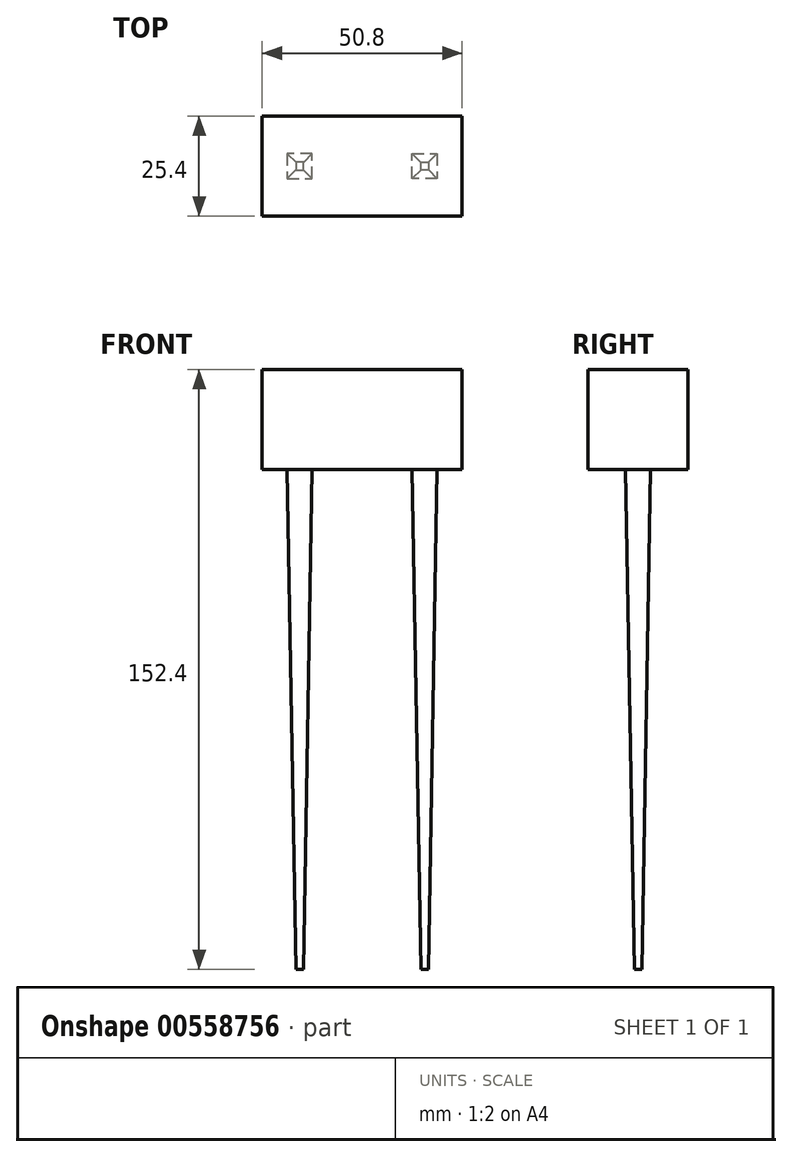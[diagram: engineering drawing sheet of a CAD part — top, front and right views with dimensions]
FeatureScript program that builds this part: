
annotation { "Feature Type Name" : "Feature", "Feature Type Description" : "" }
export const myFeature = defineFeature(function(context is Context, id is Id, definition is map)
    precondition{}
    {
        {
            var Q0;
            Q0=qCreatedBy(makeId("Top.planeOp"),FACE);
            var sketch = newSketch(context, id + "F0", { "sketchPlane" : qUnion([Q0])});
            skLineSegment(sketch, "E0.bottom", {"start": v(-25.4, 12.7) * mm, "end": v(25.4, 12.7) * mm});
            skLineSegment(sketch, "E0.top", {"start": v(-25.4, -12.7) * mm, "end": v(25.4, -12.7) * mm});
            skLineSegment(sketch, "E0.left", {"start": v(-25.4, 12.7) * mm, "end": v(-25.4, -12.7) * mm});
            skLineSegment(sketch, "E0.right", {"start": v(25.4, 12.7) * mm, "end": v(25.4, -12.7) * mm});
            skSolve(sketch);
        }
        {
            var Q0;
            Q0=makeQuery(id+"F0.imprint","IMPRINT",FACE,{"disambiguationData":[TD([[makeQuery(id+"F0.imprint","IMPRINT",EDGE,{"derivedFrom":sQuery(id+"F0.wireOp",EDGE,"E0.bottom")}),-1.0]])]});
            extrude(context, id + "F1", {"entities" : qUnion([Q0]), "oppositeDirection" : true, "depth" : 25.4 * mm, "offsetDistance" : 25.4 * mm});
        }
        {
            var Q0;
            Q0=makeQuery(id+"F1.opExtrude","CAP_FACE",FACE,{"disambiguationData":[OSD([sQuery(id+"F0.wireOp",EDGE,"E0.bottom"),sQuery(id+"F0.wireOp",EDGE,"E0.top"),sQuery(id+"F0.wireOp",EDGE,"E0.left"),sQuery(id+"F0.wireOp",EDGE,"E0.right")])],"isStart":false});
            var sketch = newSketch(context, id + "F2", { "sketchPlane" : qUnion([Q0])});
            skLineSegment(sketch, "E1.bottom", {"start": v(-19.05, 3.18) * mm, "end": v(-12.7, 3.18) * mm});
            skLineSegment(sketch, "E1.top", {"start": v(-19.05, -3.18) * mm, "end": v(-12.7, -3.18) * mm});
            skLineSegment(sketch, "E1.left", {"start": v(-19.05, 3.18) * mm, "end": v(-19.05, -3.18) * mm});
            skLineSegment(sketch, "E1.right", {"start": v(-12.7, 3.18) * mm, "end": v(-12.7, -3.18) * mm});
            skSolve(sketch);
        }
        {
            var Q0;
            Q0=makeQuery(id+"F2.imprint","IMPRINT",FACE,{"disambiguationData":[TD([[makeQuery(id+"F2.imprint","IMPRINT",EDGE,{"derivedFrom":sQuery(id+"F2.wireOp",EDGE,"E1.bottom")}),-1.0]])]});
            extrude(context, id + "F3", {"entities" : qUnion([Q0]), "depth" : 127 * mm, "offsetDistance" : 25.4 * mm, "hasDraft" : true, "draftAngle" : 1 * degree, "draftPullDirection" : true});
        }
        {
            var Q0;
            Q0=makeQuery(id+"F3.opExtrude","SWEPT_BODY",BODY,{"disambiguationData":[OSD([sQuery(id+"F2.wireOp",EDGE,"E1.bottom"),sQuery(id+"F2.wireOp",EDGE,"E1.top"),sQuery(id+"F2.wireOp",EDGE,"E1.left"),sQuery(id+"F2.wireOp",EDGE,"E1.right")])]});
            var Q1;
            Q1=qCreatedBy(makeId("Right.planeOp"),FACE);
            mirror(context, id + "F4", {"entities" : qUnion([Q0]), "mirrorPlane" : qUnion([Q1])});
        }
    });
